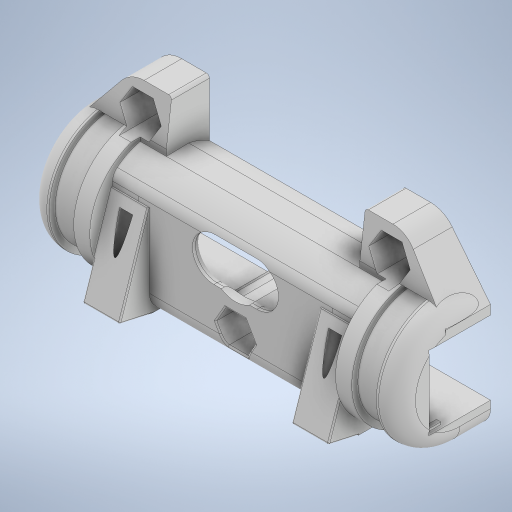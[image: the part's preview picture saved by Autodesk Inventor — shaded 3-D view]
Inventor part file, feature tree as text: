
AUTODESK INVENTOR PART (.ipt)
format: ipt  version: 2023 (Build 270158000, 158)  size: 2,009,088 bytes
history: native  units: mm
features: extrude x61, projected_geometry x60, sketch x41, fillet x6, mirror x3, plane x2
ambient origin geometry x8: Origin, YZ Plane, XZ Plane, XY Plane, X Axis, Y Axis, Z Axis, Center Point
bodies: Solid1 (feature_tree)
feature tree (173):
  extrude  "Extrusion1"  Depth=0.6mm
  extrude  "Extrusion2"  Depth=5.1mm
  extrude  "Extrusion3"  Depth=11.5mm TaperAngle=0.0deg
  extrude  "Extrusion4"  Depth=1.0mm
  extrude  "Extrusion5"  Depth=2.5mm TaperAngle=0.0deg
  mirror  "Mirror1"
  extrude  "Extrusion6"  Depth=30.0mm TaperAngle=0.0deg
  extrude  "Extrusion7"  Depth=3.5mm
  extrude  "Extrusion8"  Depth=37.5mm
  extrude  "Extrusion9"  Depth=1.5mm
  extrude  "Extrusion10"  Depth=4.0mm TaperAngle=0.0deg
  fillet  "Fillet1"  Radius=2.75mm
  extrude  "Extrusion11"  Depth=2.7mm
  sketch  "Sketch13"  dims[d37=2.0mm d38=0.0mm d39=3.0mm d40=0.0mm]
  extrude  "Extrusion12"  Depth=3.0mm TaperAngle=0.0deg
  extrude  "Extrusion13"  Depth=0.5mm
  extrude  "Extrusion14"  Depth=5.0mm
  extrude  "Extrusion15"  Depth=2.0mm TaperAngle=0.0deg
  extrude  "Extrusion16"  Depth=5.0mm
  extrude  "Extrusion17"  Depth=1.0mm
  extrude  "Extrusion18"  Depth=14.25mm TaperAngle=0.0deg
  sketch  "Sketch14"  dims[d41=7.0mm d42=0.0mm d43=0.5mm]
  extrude  "Extrusion19"  Depth=14.25mm TaperAngle=0.0deg
  extrude  "Extrusion20"  Depth=14.25mm TaperAngle=0.0deg
  plane  "Work Plane1"
  extrude  "Extrusion21"  Depth=2.5mm TaperAngle=0.0deg
  extrude  "Extrusion22"  Depth=4.0mm TaperAngle=0.0deg
  sketch  "Sketch17"  dims[d49=30.4mm d52=5.0mm]
  extrude  "Extrusion23"  Depth=14.25mm TaperAngle=0.0deg
  extrude  "Extrusion24"  Depth=14.25mm TaperAngle=0.0deg
  extrude  "Extrusion25"  Depth=14.25mm TaperAngle=0.0deg
  fillet  "Fillet3"  Radius=0.5mm
  extrude  "Extrusion26"  Depth=10.0mm TaperAngle=0.0deg
  extrude  "Extrusion27"  TaperAngle=0.0deg  [1 undecoded]
  extrude  "Extrusion28"  TaperAngle=0.0deg  [1 undecoded]
  extrude  "Extrusion29"  Depth=3.0mm TaperAngle=0.0deg
  extrude  "Extrusion30"  TaperAngle=0.0deg  [1 undecoded]
  sketch  "Sketch24"  dims[d75=2.5mm d76=0.0mm d77=14.25mm d78=0.0mm]
  extrude  "Extrusion31"  Depth=10.0mm TaperAngle=0.0deg
  extrude  "Extrusion32"  Depth=10.0mm TaperAngle=0.0deg
  sketch  "Sketch25"  dims[d79=14.25mm d80=0.0mm d82=14.25mm d83=0.0mm]
  extrude  "Extrusion33"  Depth=7.5mm TaperAngle=0.0deg
  extrude  "Extrusion34"  TaperAngle=0.0deg  [1 undecoded]
  extrude  "Extrusion35"  Depth=22.0mm TaperAngle=0.0deg
  extrude  "Extrusion36"  Depth=10.0mm TaperAngle=0.0deg
  sketch  "Sketch26"  dims[d84=2.0mm d85=14.25mm d86=0.0mm d87=0.5mm]
  extrude  "Extrusion37"  Depth=10.0mm TaperAngle=0.0deg
  extrude  "Extrusion38"  Depth=4.0mm TaperAngle=0.0deg
  extrude  "Extrusion39"  Depth=29.237756mm
  extrude  "Extrusion40"  Depth=6.0mm TaperAngle=0.0deg
  mirror  "Mirror2"
  extrude  "Extrusion41"  Depth=10.0mm
  fillet  "Fillet4"  Radius=13.0mm
  extrude  "Extrusion42"  Depth=10.0mm
  extrude  "Extrusion43"  Depth=10.0mm
  extrude  "Extrusion44"  TaperAngle=0.0deg  [1 undecoded]
  sketch  "Sketch34"  dims[d113=10.0mm d114=0.0mm d115=1.0mm d116=0.0mm]
  extrude  "Extrusion47"  Depth=10.0mm
  extrude  "Extrusion48"  Depth=10.0mm
  extrude  "Extrusion49"  Depth=10.0mm TaperAngle=0.0deg
  sketch  "Sketch35"  dims[d117=7.5mm d118=0.0mm d119=7.5mm d120=0.0mm]
  extrude  "Extrusion50"  TaperAngle=0.0deg  [1 undecoded]
  extrude  "Extrusion51"  Depth=10.0mm TaperAngle=0.0deg
  extrude  "Extrusion52"  Depth=10.0mm TaperAngle=0.0deg
  extrude  "Extrusion53"  TaperAngle=0.0deg  [1 undecoded]
  sketch  "Sketch38"  dims[d133=10.0mm d134=0.0mm d135=7.375mm d136=0.0mm]
  extrude  "Extrusion54"  Depth=10.0mm
  extrude  "Extrusion55"  Depth=10.0mm
  extrude  "Extrusion56"  Depth=10.0mm
  extrude  "Extrusion57"  Depth=10.0mm TaperAngle=0.0deg
  sketch  "Sketch41"  dims[d145=15.75mm d146=0.0mm d147=29.237756mm]
  extrude  "Extrusion58"  [1 undecoded]
  extrude  "Extrusion59"  [1 undecoded]
  extrude  "Extrusion60"  [1 undecoded]
  sketch  "Sketch42"  dims[d148=5.0mm d149=6.0mm d150=0.0mm]
  extrude  "Extrusion61"  [1 undecoded]
  extrude  "Extrusion62"  [1 undecoded]
  fillet  "Fillet5"  [1 undecoded]
  fillet  "Fillet6"  [1 undecoded]
  fillet  "Fillet7"  [1 undecoded]
  extrude  "Extrusion63"  [1 undecoded]
  mirror  "Mirror3"
  sketch  "Sketch1"  dims[d0=11.5mm d1=0.0mm d2=0.6mm]
  sketch  "Sketch2"  dims[d3=0.7mm d4=5.1mm]
  projected_geometry  "Projected Loop1"
  projected_geometry  "Projected Loop2"
  sketch  "Sketch3"  dims[d5=2.0mm d6=11.5mm d7=0.0mm]
  sketch  "Sketch4"  dims[d8=1.0mm d9=1.0mm]
  sketch  "Sketch6"  dims[d10=1.0mm d11=2.5mm d12=0.0mm]
  projected_geometry  "Projected Loop3"
  sketch  "Sketch7"  dims[d13=0.1mm d14=0.0mm d21=30.0mm d22=0.0mm]
  projected_geometry  "Projected Loop4"
  projected_geometry  "Projected Loop5"
  projected_geometry  "Projected Loop6"
  sketch  "Sketch8"  dims[d23=44.0mm d24=3.5mm]
  projected_geometry  "Projected Loop7"
  projected_geometry  "Projected Loop8"
  sketch  "Sketch9"  dims[d25=3.0mm d27=37.5mm]
  projected_geometry  "Projected Loop9"
  sketch  "Sketch10"  dims[d28=1.5mm d29=1.5mm]
  projected_geometry  "Projected Loop10"
  sketch  "Sketch11"  dims[d30=3.0mm d31=4.0mm d32=0.0mm d33=2.75mm d34=0.0mm]
  projected_geometry  "Projected Loop11"
  sketch  "Sketch12"  dims[d35=2.7mm d36=2.7mm]
  projected_geometry  "Projected Loop12"
  projected_geometry  "Projected Loop13"
  projected_geometry  "Projected Loop14"
  projected_geometry  "Projected Loop15"
  projected_geometry  "Projected Loop16"
  projected_geometry  "Projected Loop17"
  projected_geometry  "Projected Loop18"
  sketch  "Sketch15"  dims[d44=31.0mm d45=5.0mm]
  sketch  "Sketch16"  dims[d46=3.0mm d47=2.0mm d48=0.0mm]
  projected_geometry  "Projected Loop19"
  projected_geometry  "Projected Loop20"
  projected_geometry  "Projected Loop21"
  projected_geometry  "Projected Loop22"
  sketch  "Sketch18"  dims[d53=2.0mm d54=1.0mm]
  projected_geometry  "Projected Loop23"
  sketch  "Sketch19"  dims[d55=15.0mm d56=0.0mm d57=14.25mm d58=0.0mm]
  projected_geometry  "Projected Loop24"
  projected_geometry  "Projected Loop25"
  sketch  "Sketch20"  dims[d59=14.25mm d60=0.0mm d61=14.25mm d62=0.0mm]
  projected_geometry  "Projected Loop26"
  sketch  "Sketch21"  dims[d63=14.25mm d64=0.0mm d65=14.25mm d66=0.0mm]
  projected_geometry  "Projected Loop27"
  projected_geometry  "Projected Loop28"
  sketch  "Sketch22"  dims[d67=2.5mm d68=0.0mm d69=2.5mm d70=0.0mm]
  projected_geometry  "Projected Loop29"
  sketch  "Sketch23"  dims[d71=2.5mm d72=0.0mm d73=4.0mm d74=0.0mm]
  projected_geometry  "Projected Loop30"
  projected_geometry  "Projected Loop31"
  projected_geometry  "Projected Loop32"
  projected_geometry  "Projected Loop33"
  projected_geometry  "Projected Loop34"
  projected_geometry  "Projected Loop35"
  projected_geometry  "Projected Loop36"
  sketch  "Sketch27"  dims[d88=0.0mm d89=0.0mm d90=10.0mm d91=0.0mm]
  projected_geometry  "Projected Loop37"
  sketch  "Sketch28"  dims[d92=0.0mm d93=0.0mm d94=0.0mm d95=0.0mm]
  projected_geometry  "Projected Loop38"
  plane  "Work Plane2"
  sketch  "Sketch29"  dims[d96=1.0mm d97=0.0mm d98=0.0mm d99=0.0mm]
  projected_geometry  "Projected Loop39"
  sketch  "Sketch30"  dims[d100=8.0mm d101=0.0mm d102=3.0mm d103=0.0mm]
  projected_geometry  "Projected Loop40"
  projected_geometry  "Projected Loop41"
  sketch  "Sketch31"  dims[d104=1.75mm d105=2.25mm d106=0.0mm d107=0.0mm d108=0.0mm d109=0.0mm]
  projected_geometry  "Projected Loop42"
  projected_geometry  "Projected Loop43"
  sketch  "Sketch32"  dims[d110=3.5mm d111=10.0mm d112=0.0mm]
  projected_geometry  "Projected Loop45"
  projected_geometry  "Projected Loop46"
  projected_geometry  "Projected Loop47"
  projected_geometry  "Projected Loop48"
  projected_geometry  "Projected Loop49"
  sketch  "Sketch36"  dims[d121=0.2mm d122=0.0mm d123=0.0mm]
  projected_geometry  "Projected Loop50"
  sketch  "Sketch37"  dims[d124=6.0mm d125=0.0mm d126=22.0mm d127=0.0mm]
  projected_geometry  "Projected Loop51"
  projected_geometry  "Projected Loop52"
  projected_geometry  "Projected Loop53"
  sketch  "Sketch39"  dims[d137=3.375mm d138=0.0mm d139=10.0mm d140=0.0mm]
  projected_geometry  "Projected Loop54"
  sketch  "Sketch40"  dims[d141=5.0mm d142=0.0mm d143=4.0mm d144=0.0mm]
  projected_geometry  "Projected Loop55"
  projected_geometry  "Projected Loop56"
  projected_geometry  "Projected Loop57"
  projected_geometry  "Projected Loop58"
  projected_geometry  "Projected Loop59"
  projected_geometry  "Projected Loop60"
  sketch  "Sketch43"  dims[d151=8.0mm d152=0.0mm d153=2.5mm d154=13.0mm d155=0.0mm d156=6.0mm d157=7.0mm d158=0.0mm d159=0.0mm d160=3.0mm d161=2.8mm d162=11.5mm d163=0.0mm d164=0.0mm d165=0.0mm d166=7.8mm d167=0.0mm d168=10.0mm d169=0.0mm d170=0.0mm d171=0.0mm d172=3.0mm d173=0.2mm d174=1.0mm d175=0.25mm d176=0.0mm]
  projected_geometry  "Projected Loop61"
note: 16 required parameter values undecoded (feature->parameter linkage not recoverable at this tier; creation-order binding heuristic only, values carry confidence <= 0.55)
